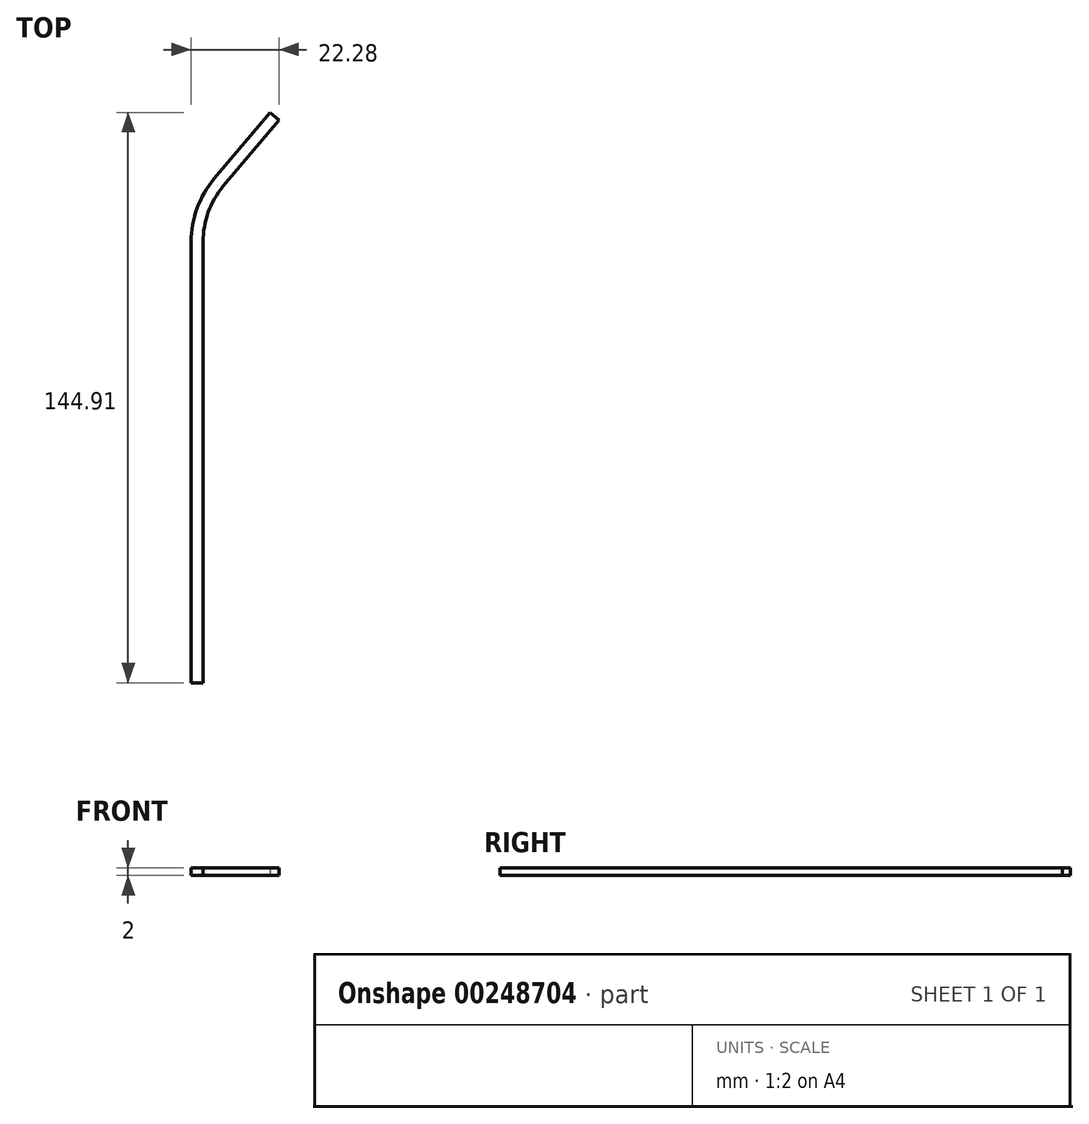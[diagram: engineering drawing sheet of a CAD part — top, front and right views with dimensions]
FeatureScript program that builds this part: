
annotation { "Feature Type Name" : "Feature", "Feature Type Description" : "" }
export const myFeature = defineFeature(function(context is Context, id is Id, definition is map)
    precondition{}
    {
        {
            var Q0;
            Q0=qCreatedBy(makeId("Top.planeOp"),FACE);
            var sketch = newSketch(context, id + "F0", { "sketchPlane" : qUnion([Q0])});
            skLineSegment(sketch, "E0", {"start": v(0, 0) * mm, "end": v(0, 112) * mm});
            skLineSegment(sketch, "E1", {"start": v(5.15, 126.13) * mm, "end": v(19.28, 142.98) * mm});
            skPoint(sketch, "E2.visualSharp", {"position": v(0, 120) * mm});
            skArc(sketch, "E2.filletArc", {"start": v(5.15, 126.13) * mm, "mid": v(1.33, 119.52) * mm, "end": v(0, 112) * mm});
            skLineSegment(sketch, "E3.0", {"start": v(2.85, 128.06) * mm, "end": v(16.99, 144.9) * mm});
            skArc(sketch, "E3.1", {"start": v(2.85, 128.06) * mm, "mid": v(-1.5, 120.54) * mm, "end": v(-3, 112) * mm});
            skLineSegment(sketch, "E3.2", {"start": v(-3, 0) * mm, "end": v(-3, 112) * mm});
            skLineSegment(sketch, "E4", {"start": v(16.99, 144.9) * mm, "end": v(19.28, 142.98) * mm});
            skLineSegment(sketch, "E5", {"start": v(-3, 0) * mm, "end": v(0, 0) * mm});
            skSolve(sketch);
        }
        {
            var Q0;
            Q0=qSketchRegion(id+"F0",true);
            extrude(context, id + "F1", {"entities" : qUnion([Q0]), "depth" : 2 * mm});
        }
    });
